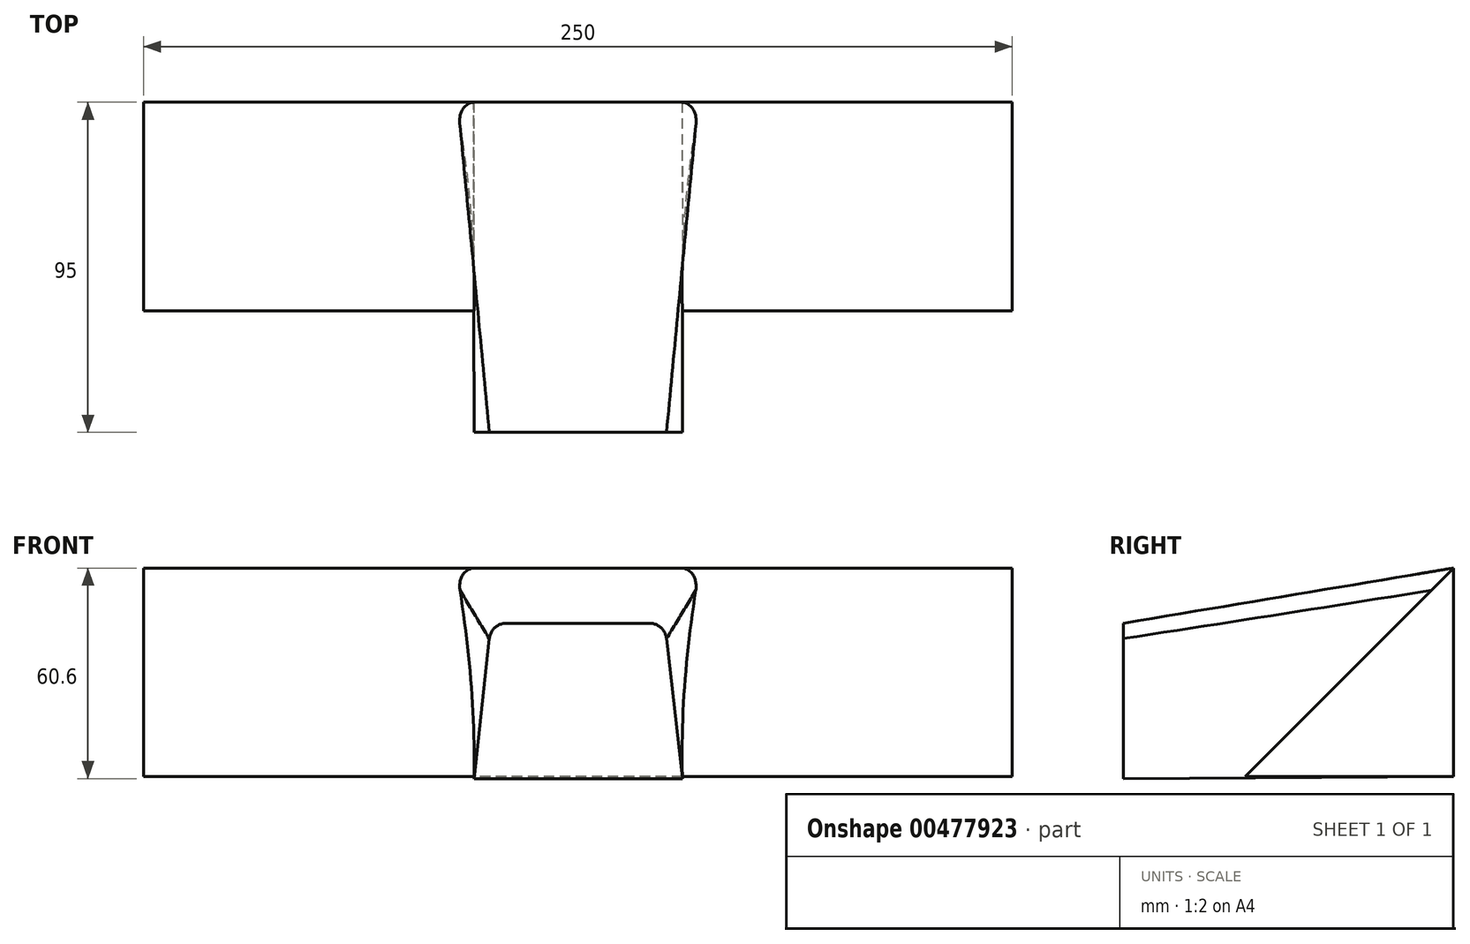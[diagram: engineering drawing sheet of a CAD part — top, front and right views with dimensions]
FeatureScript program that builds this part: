
annotation { "Feature Type Name" : "Feature", "Feature Type Description" : "" }
export const myFeature = defineFeature(function(context is Context, id is Id, definition is map)
    precondition{}
    {
        {
            var Q0;
            Q0=qCreatedBy(makeId("Front.planeOp"),FACE);
            var sketch = newSketch(context, id + "F0", { "sketchPlane" : qUnion([Q0])});
            skLineSegment(sketch, "E0.bottom", {"start": v(125, 30) * mm, "end": v(-125, 30) * mm});
            skLineSegment(sketch, "E0.top", {"start": v(125, -30) * mm, "end": v(-125, -30) * mm});
            skLineSegment(sketch, "E0.left", {"start": v(125, 30) * mm, "end": v(125, -30) * mm});
            skLineSegment(sketch, "E0.right", {"start": v(-125, 30) * mm, "end": v(-125, -30) * mm});
            skPoint(sketch, "E0.middle", {"position": v(0, 0) * mm});
            skSolve(sketch);
        }
        {
            var Q0;
            Q0=makeQuery(id+"F0.imprint","IMPRINT",FACE,{"disambiguationData":[TD([[makeQuery(id+"F0.imprint","IMPRINT",EDGE,{"derivedFrom":sQuery(id+"F0.wireOp",EDGE,"E0.bottom")}),1.0]])]});
            extrude(context, id + "F1", {"entities" : qUnion([Q0]), "depth" : 60 * mm});
        }
        {
            var Q0;
            Q0=makeQuery(id+"F1.opExtrude","SWEPT_FACE",FACE,{"disambiguationData":[OSD([sQuery(id+"F0.wireOp",EDGE,"E0.left")])]});
            var sketch = newSketch(context, id + "F2", { "sketchPlane" : qUnion([Q0])});
            skLineSegment(sketch, "E1", {"start": v(0, 30) * mm, "end": v(-60, -30) * mm});
            skSolve(sketch);
        }
        {
            var Q0;
            Q0=makeQuery(id+"F2.imprint","IMPRINT",FACE,{"disambiguationData":[TD([[makeQuery(id+"F2.imprint","IMPRINT",EDGE,{"derivedFrom":sQuery(id+"F2.wireOp",EDGE,"E1")}),-1.0]])]});
            extrude(context, id + "F3", {"entities" : qUnion([Q0]), "operationType" : NewBodyOperationType.REMOVE, "oppositeDirection" : true, "depth" : 250 * mm});
        }
        {
            var Q0;
            Q0=makeQuery(id+"F1.opExtrude","CAP_FACE",FACE,{"disambiguationData":[OSD([sQuery(id+"F0.wireOp",EDGE,"E0.bottom"),sQuery(id+"F0.wireOp",EDGE,"E0.top"),sQuery(id+"F0.wireOp",EDGE,"E0.left"),sQuery(id+"F0.wireOp",EDGE,"E0.right")])],"isStart":true});
            var sketch = newSketch(context, id + "F4", { "sketchPlane" : qUnion([Q0])});
            skLineSegment(sketch, "E2", {"start": v(-35, 30) * mm, "end": v(-30, -30) * mm});
            skLineSegment(sketch, "E3", {"start": v(35, 30) * mm, "end": v(30, -30) * mm});
            skSolve(sketch);
        }
        {
            var Q0;
            Q0=qCreatedBy(makeId("Front.planeOp"),FACE);
            cPlane(context, id + "F5", {"entities" : qUnion([Q0]), "cplaneType" : CPlaneType.OFFSET, "offset" : 95 * mm, "width" : 150 * mm, "height" : 150 * mm});
        }
        {
            var Q0;
            Q0=qCreatedBy(id+"F5.planeOp",FACE);
            var sketch = newSketch(context, id + "F6", { "sketchPlane" : qUnion([Q0])});
            skLineSegment(sketch, "E4", {"start": v(-25, 14.12) * mm, "end": v(25, 14.12) * mm});
            skLineSegment(sketch, "E5", {"start": v(-25, 14.12) * mm, "end": v(-29.86, -30.6) * mm});
            skLineSegment(sketch, "E6", {"start": v(25, 14.12) * mm, "end": v(30.14, -30.6) * mm});
            skLineSegment(sketch, "E7", {"start": v(-29.86, -30.6) * mm, "end": v(30.14, -30.6) * mm});
            skSolve(sketch);
        }
        {
            var Q1;
            {var subQ0=sQuery(id+"F4.wireOp",EDGE,"E2");Q1=makeQuery(id+"F4.imprint","IMPRINT",FACE,{"disambiguationData":[TD([[makeQuery(id+"F4.imprint","IMPRINT",EDGE,{"derivedFrom":subQ0}),1.0]])]});}
            var Q2;
            Q2=makeQuery(id+"F6.imprint","IMPRINT",FACE,{"disambiguationData":[TD([[makeQuery(id+"F6.imprint","IMPRINT",EDGE,{"derivedFrom":sQuery(id+"F6.wireOp",EDGE,"E4")}),-1.0]])]});
            loft(context, id + "F7", {"operationType" : NewBodyOperationType.ADD, "sheetProfilesArray" : [{ "sheetProfileEntities" : qUnion([Q1]) }, { "sheetProfileEntities" : qUnion([Q2]) }]});
        }
        {
            var Q0;
            Q0=makeQuery(id+"F7.opLoft","SWEPT_EDGE",EDGE,{"disambiguationData":[OSD([sQuery(id+"F0.wireOp",EDGE,"E0.bottom"),sQuery(id+"F0.wireOp",EDGE,"E0.left"),sQuery(id+"F2.wireOp",EDGE,"E1"),sQuery(id+"F4.wireOp",EDGE,"E2"),sQuery(id+"F6.wireOp",EDGE,"E4"),sQuery(id+"F6.wireOp",EDGE,"E6")])]});
            var Q1;
            Q1=makeQuery(id+"F7.opLoft","SWEPT_EDGE",EDGE,{"disambiguationData":[OSD([sQuery(id+"F0.wireOp",EDGE,"E0.bottom"),sQuery(id+"F0.wireOp",EDGE,"E0.left"),sQuery(id+"F2.wireOp",EDGE,"E1"),sQuery(id+"F4.wireOp",EDGE,"E3"),sQuery(id+"F6.wireOp",EDGE,"E4"),sQuery(id+"F6.wireOp",EDGE,"E5")])]});
            fillet(context, id + "F8", {"entities" : qUnion([Q0, Q1]), "radius" : 5 * mm, "tangentPropagation" : true, "allowEdgeOverflow" : false});
        }
    });
